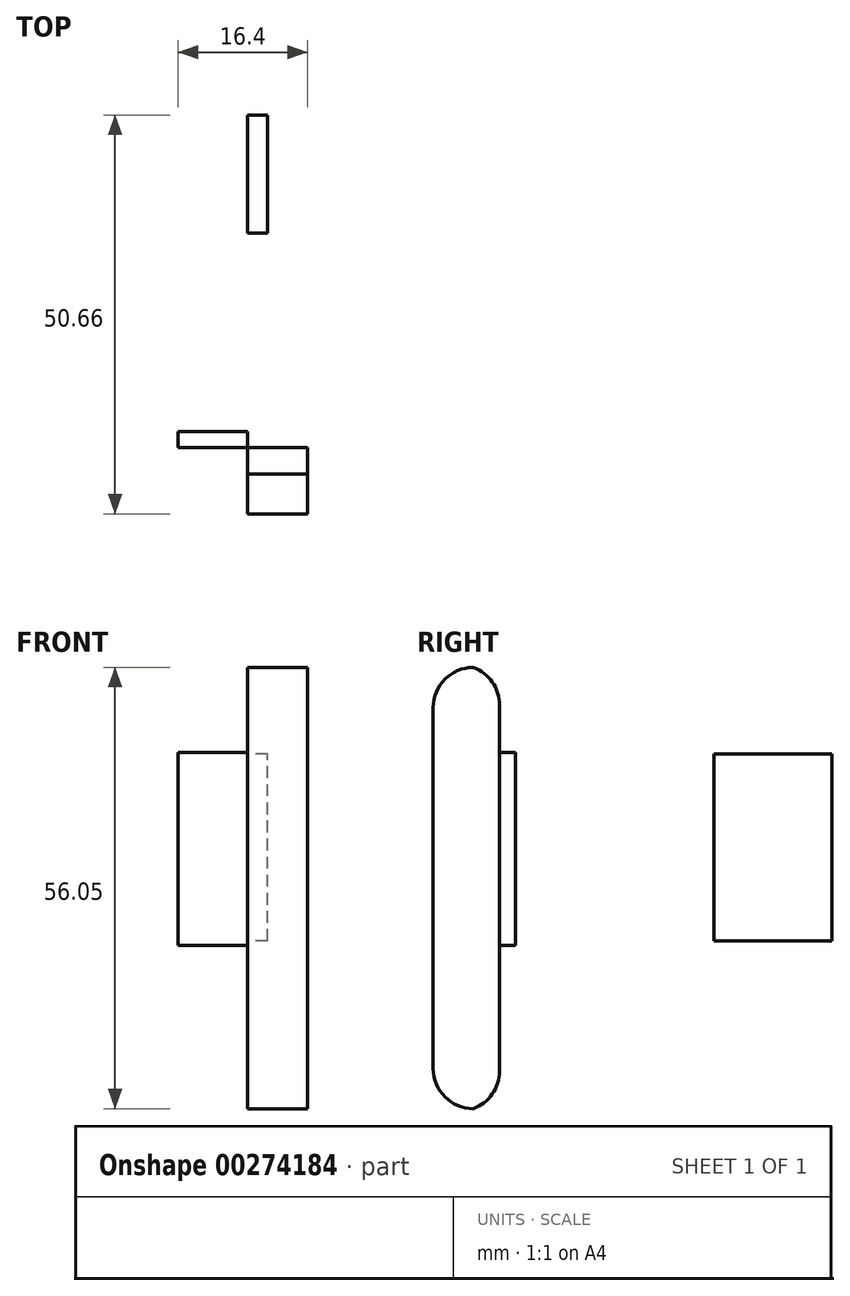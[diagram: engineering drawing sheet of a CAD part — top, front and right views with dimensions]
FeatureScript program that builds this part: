
annotation { "Feature Type Name" : "Feature", "Feature Type Description" : "" }
export const myFeature = defineFeature(function(context is Context, id is Id, definition is map)
    precondition{}
    {
        {
            var Q0;
            Q0=qCreatedBy(makeId("Right.planeOp"),FACE);
            var sketch = newSketch(context, id + "F0", { "sketchPlane" : qUnion([Q0])});
            skLineSegment(sketch, "E0.bottom", {"start": v(0, 0) * mm, "end": v(-8.41, 0) * mm});
            skLineSegment(sketch, "E0.top", {"start": v(0, 56.05) * mm, "end": v(-8.41, 56.05) * mm});
            skLineSegment(sketch, "E0.left", {"start": v(0, 0) * mm, "end": v(0, 56.05) * mm});
            skLineSegment(sketch, "E0.right", {"start": v(-8.41, 0) * mm, "end": v(-8.41, 56.05) * mm});
            skSolve(sketch);
        }
        {
            var Q0;
            Q0=makeQuery(id+"F0.imprint","IMPRINT",FACE,{"disambiguationData":[TD([[makeQuery(id+"F0.imprint","IMPRINT",EDGE,{"derivedFrom":sQuery(id+"F0.wireOp",EDGE,"E0.bottom")}),-1.0]])]});
            extrude(context, id + "F1", {"entities" : qUnion([Q0]), "depth" : 7.62 * mm});
        }
        {
            var Q0;
            Q0=makeQuery(id+"F1.opExtrude","SWEPT_EDGE",EDGE,{"disambiguationData":[OSD([sQuery(id+"F0.wireOp",EDGE,"E0.top"),sQuery(id+"F0.wireOp",EDGE,"E0.right")])]});
            fillet(context, id + "F2", {"entities" : qUnion([Q0]), "radius" : 5.08 * mm, "tangentPropagation" : true, "allowEdgeOverflow" : false});
        }
        {
            var Q0;
            Q0=makeQuery(id+"F1.opExtrude","SWEPT_EDGE",EDGE,{"disambiguationData":[OSD([sQuery(id+"F0.wireOp",EDGE,"E0.top"),sQuery(id+"F0.wireOp",EDGE,"E0.left")])]});
            fillet(context, id + "F3", {"entities" : qUnion([Q0]), "radius" : 5.08 * mm, "tangentPropagation" : true, "allowEdgeOverflow" : false});
        }
        {
            var Q0;
            Q0=makeQuery(id+"F1.opExtrude","SWEPT_EDGE",EDGE,{"disambiguationData":[OSD([sQuery(id+"F0.wireOp",EDGE,"E0.bottom"),sQuery(id+"F0.wireOp",EDGE,"E0.right")])]});
            fillet(context, id + "F4", {"entities" : qUnion([Q0]), "radius" : 5.08 * mm, "tangentPropagation" : true, "allowEdgeOverflow" : false});
        }
        {
            var Q0;
            Q0=makeQuery(id+"F1.opExtrude","SWEPT_EDGE",EDGE,{"disambiguationData":[OSD([sQuery(id+"F0.wireOp",EDGE,"E0.bottom"),sQuery(id+"F0.wireOp",EDGE,"E0.left")])]});
            fillet(context, id + "F5", {"entities" : qUnion([Q0]), "radius" : 5.08 * mm, "tangentPropagation" : true, "allowEdgeOverflow" : false});
        }
        {
            var Q0;
            Q0=qCreatedBy(makeId("Right.planeOp"),FACE);
            var sketch = newSketch(context, id + "F6", { "sketchPlane" : qUnion([Q0])});
            skLineSegment(sketch, "E1.bottom", {"start": v(27.25, 21.3) * mm, "end": v(42.25, 21.3) * mm});
            skLineSegment(sketch, "E1.top", {"start": v(27.25, 45.08) * mm, "end": v(42.25, 45.08) * mm});
            skLineSegment(sketch, "E1.left", {"start": v(27.25, 21.3) * mm, "end": v(27.25, 45.08) * mm});
            skLineSegment(sketch, "E1.right", {"start": v(42.25, 21.3) * mm, "end": v(42.25, 45.08) * mm});
            skSolve(sketch);
        }
        {
            var Q0;
            Q0=makeQuery(id+"F6.imprint","IMPRINT",FACE,{"disambiguationData":[TD([[makeQuery(id+"F6.imprint","IMPRINT",EDGE,{"derivedFrom":sQuery(id+"F6.wireOp",EDGE,"E1.bottom")}),1.0]])]});
            extrude(context, id + "F7", {"entities" : qUnion([Q0]), "depth" : 2.54 * mm});
        }
        {
            var Q0;
            Q0=qCreatedBy(makeId("Front.planeOp"),FACE);
            var sketch = newSketch(context, id + "F8", { "sketchPlane" : qUnion([Q0])});
            skLineSegment(sketch, "E2.bottom", {"start": v(0, 45.26) * mm, "end": v(-8.78, 45.26) * mm});
            skLineSegment(sketch, "E2.top", {"start": v(0, 20.76) * mm, "end": v(-8.78, 20.76) * mm});
            skLineSegment(sketch, "E2.left", {"start": v(0, 45.26) * mm, "end": v(0, 20.76) * mm});
            skLineSegment(sketch, "E2.right", {"start": v(-8.78, 45.26) * mm, "end": v(-8.78, 20.76) * mm});
            skSolve(sketch);
        }
        {
            var Q0;
            Q0=makeQuery(id+"F8.imprint","IMPRINT",FACE,{"disambiguationData":[TD([[makeQuery(id+"F8.imprint","IMPRINT",EDGE,{"derivedFrom":sQuery(id+"F8.wireOp",EDGE,"E2.bottom")}),1.0]])]});
            extrude(context, id + "F9", {"entities" : qUnion([Q0]), "oppositeDirection" : true, "depth" : 1.02 * mm});
        }
        {
            var Q0;
            Q0=makeQuery(id+"F9.opExtrude","CAP_FACE",FACE,{"disambiguationData":[OSD([sQuery(id+"F8.wireOp",EDGE,"E2.bottom"),sQuery(id+"F8.wireOp",EDGE,"E2.top"),sQuery(id+"F8.wireOp",EDGE,"E2.left"),sQuery(id+"F8.wireOp",EDGE,"E2.right")])],"isStart":false});
            extrude(context, id + "F10", {"entities" : qUnion([Q0]), "operationType" : NewBodyOperationType.ADD, "depth" : 1.02 * mm});
        }
    });
